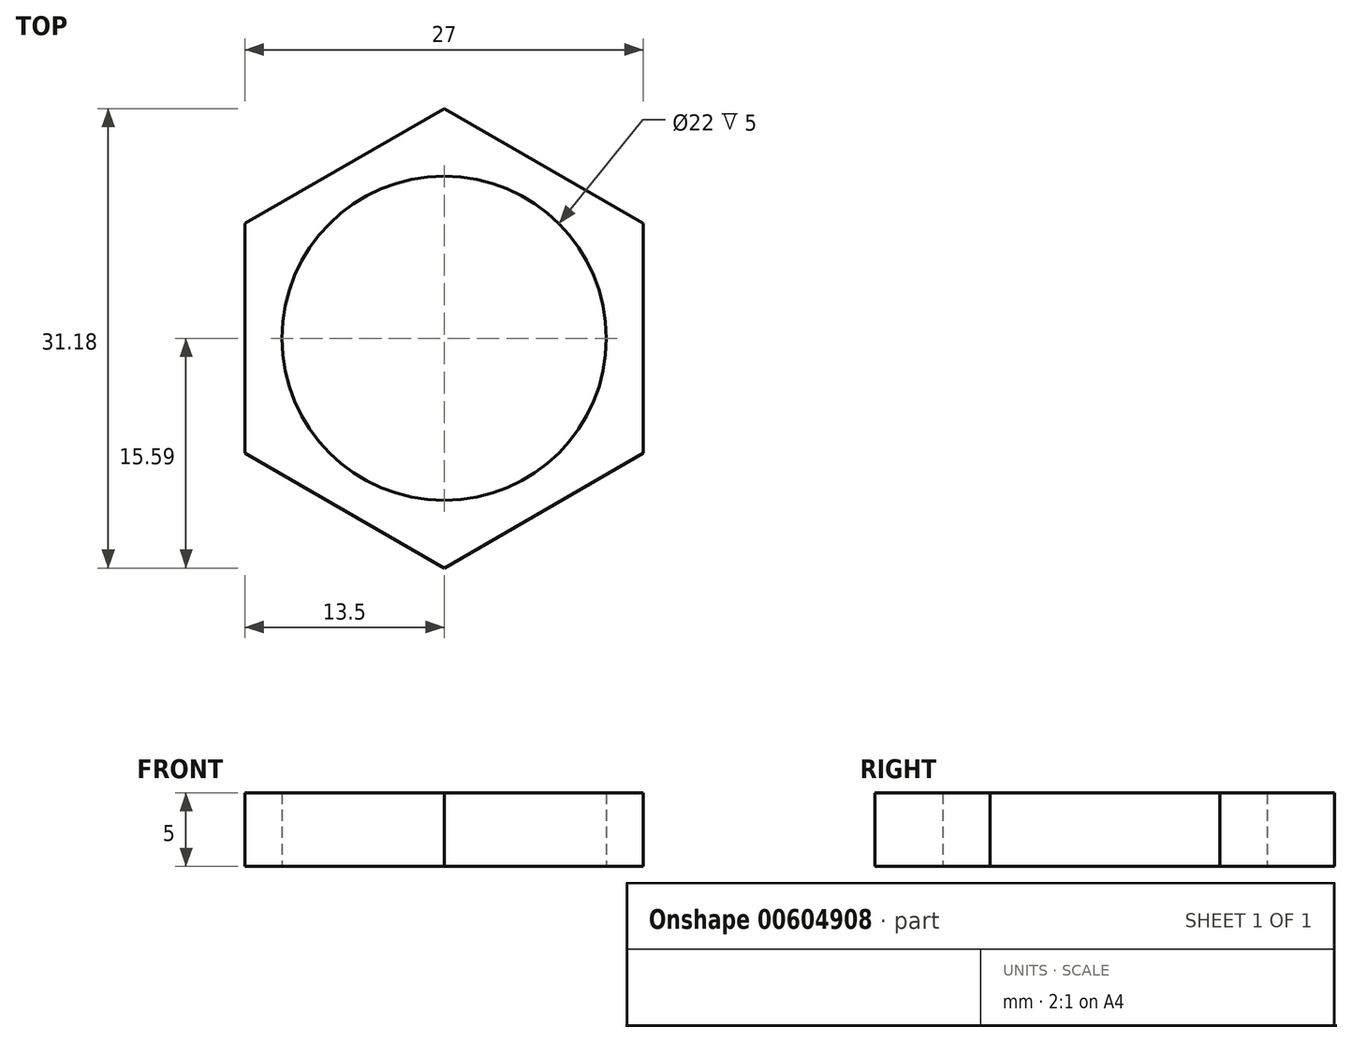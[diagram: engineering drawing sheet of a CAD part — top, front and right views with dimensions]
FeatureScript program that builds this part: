
annotation { "Feature Type Name" : "Feature", "Feature Type Description" : "" }
export const myFeature = defineFeature(function(context is Context, id is Id, definition is map)
    precondition{}
    {
        {
            var Q0;
            Q0=qCreatedBy(makeId("Top.planeOp"),FACE);
            var sketch = newSketch(context, id + "F0", { "sketchPlane" : qUnion([Q0])});
            skCircle(sketch, "E0.cCircle", {"center": v(0, 0) * mm, "radius": 13.5 * mm, "construction": true});
            skLineSegment(sketch, "E0.0", {"start": v(13.5, 7.8) * mm, "end": v(13.5, -7.8) * mm});
            skLineSegment(sketch, "E0.1", {"start": v(13.5, -7.8) * mm, "end": v(0, -15.59) * mm});
            skLineSegment(sketch, "E0.2", {"start": v(0, -15.59) * mm, "end": v(-13.5, -7.8) * mm});
            skLineSegment(sketch, "E0.3", {"start": v(-13.5, -7.8) * mm, "end": v(-13.5, 7.8) * mm});
            skLineSegment(sketch, "E0.4", {"start": v(-13.5, 7.8) * mm, "end": v(0, 15.59) * mm});
            skLineSegment(sketch, "E0.5", {"start": v(0, 15.59) * mm, "end": v(13.5, 7.8) * mm});
            skPoint(sketch, "E0.0.midPoint", {"position": v(13.5, 0) * mm});
            skCircle(sketch, "E1", {"center": v(0, 0) * mm, "radius": 11 * mm});
            skSolve(sketch);
        }
        {
            var Q0;
            Q0 = qSketchRegion(id + "F0", true);
            extrude(context, id + "F1", {"entities" : qUnion([Q0]), "depth" : 5 * mm, "offsetDistance" : 25 * mm});
        }
    });
